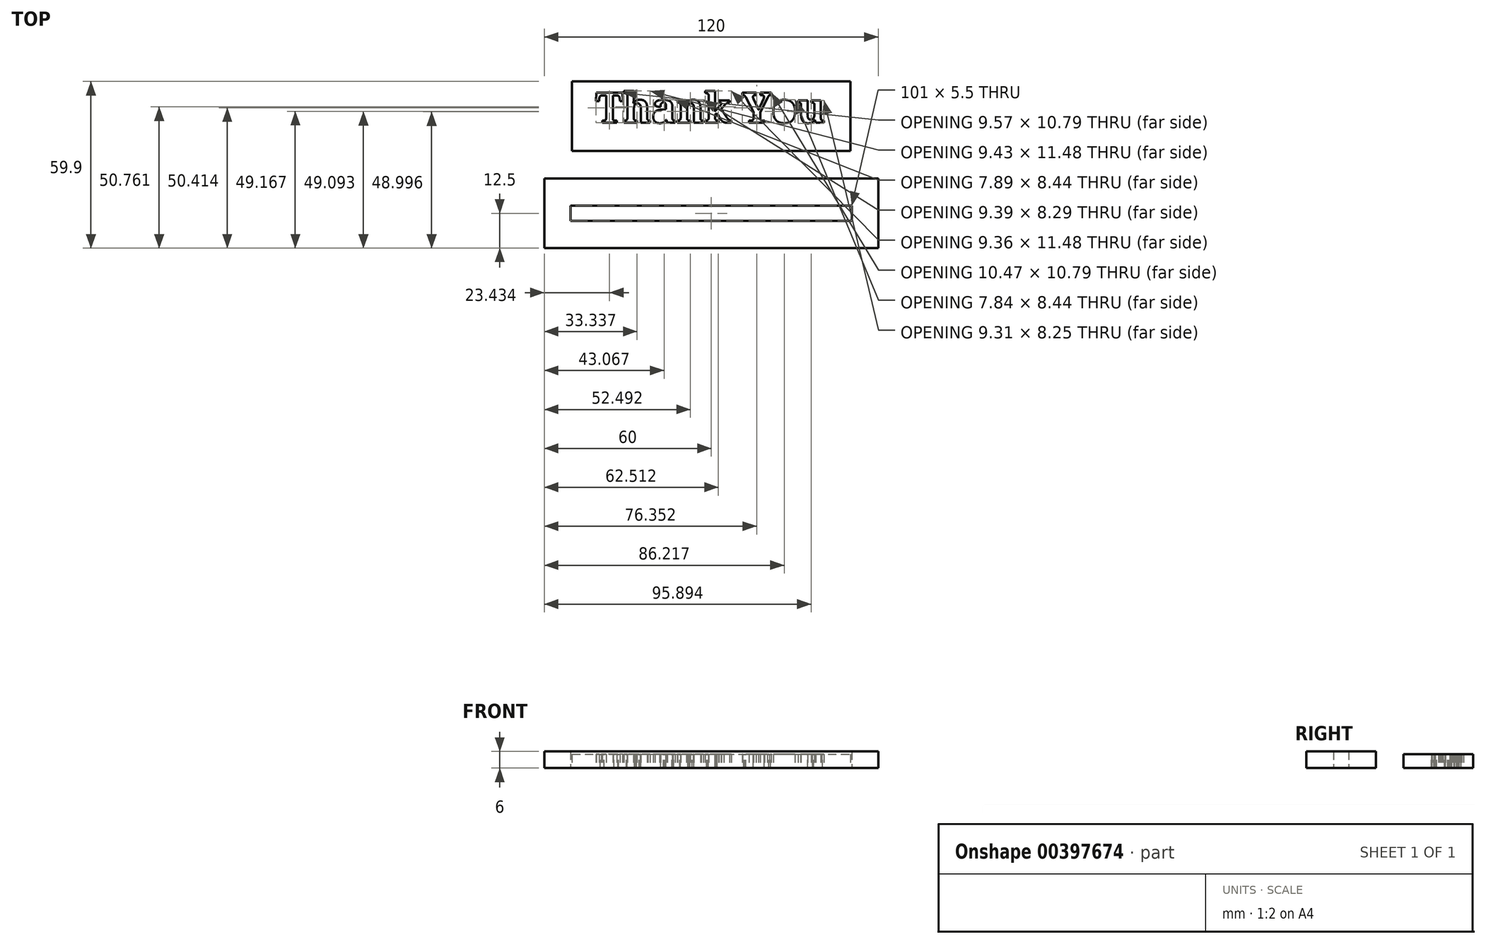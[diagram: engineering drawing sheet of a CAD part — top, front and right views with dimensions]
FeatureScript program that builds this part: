
annotation { "Feature Type Name" : "Feature", "Feature Type Description" : "" }
export const myFeature = defineFeature(function(context is Context, id is Id, definition is map)
    precondition{}
    {
        {
            var Q0;
            Q0=qCreatedBy(makeId("Top.planeOp"),FACE);
            var sketch = newSketch(context, id + "F0", { "sketchPlane" : qUnion([Q0])});
            skLineSegment(sketch, "E0.bottom", {"start": v(-50, 12.5) * mm, "end": v(50, 12.5) * mm});
            skLineSegment(sketch, "E0.top", {"start": v(-50, -12.5) * mm, "end": v(50, -12.5) * mm});
            skLineSegment(sketch, "E0.left", {"start": v(-50, 12.5) * mm, "end": v(-50, -12.5) * mm});
            skLineSegment(sketch, "E0.right", {"start": v(50, 12.5) * mm, "end": v(50, -12.5) * mm});
            skPoint(sketch, "E0.middle", {"position": v(0, 0) * mm});
            skText(sketch, "E1", { "text": "Thank You", "fontName": "NotoSerif-Bold.ttf"});
            const initialGuessF0  = {"E1": [-0.0415, -0.00238, 1, 0, 0.01088]};
            skSetInitialGuess(sketch, initialGuessF0);
            skSolve(sketch);
        }
        {
            var Q0;
            Q0 = qSketchRegion(id + "F0", true);
            extrude(context, id + "F1", {"entities" : qUnion([Q0]), "depth" : 5 * mm});
        }
        {
            var Q0;
            Q0=qCreatedBy(makeId("Top.planeOp"),FACE);
            var sketch = newSketch(context, id + "F2", { "sketchPlane" : qUnion([Q0])});
            skLineSegment(sketch, "E2.bottom", {"start": v(-60, -47.4) * mm, "end": v(60, -47.4) * mm});
            skLineSegment(sketch, "E2.top", {"start": v(-60, -22.4) * mm, "end": v(60, -22.4) * mm});
            skLineSegment(sketch, "E2.left", {"start": v(-60, -47.4) * mm, "end": v(-60, -22.4) * mm});
            skLineSegment(sketch, "E2.right", {"start": v(60, -47.4) * mm, "end": v(60, -22.4) * mm});
            skPoint(sketch, "E2.middle", {"position": v(0, -34.9) * mm});
            skLineSegment(sketch, "E3.bottom", {"start": v(-50.5, -37.65) * mm, "end": v(50.5, -37.65) * mm});
            skLineSegment(sketch, "E3.top", {"start": v(-50.5, -32.15) * mm, "end": v(50.5, -32.15) * mm});
            skLineSegment(sketch, "E3.left", {"start": v(-50.5, -37.65) * mm, "end": v(-50.5, -32.15) * mm});
            skLineSegment(sketch, "E3.right", {"start": v(50.5, -37.65) * mm, "end": v(50.5, -32.15) * mm});
            skSolve(sketch);
        }
        {
            var Q0;
            Q0=makeQuery(id+"F2.imprint","IMPRINT",FACE,{"disambiguationData":[TD([[makeQuery(id+"F2.imprint","IMPRINT",EDGE,{"derivedFrom":sQuery(id+"F2.wireOp",EDGE,"E2.bottom")}),1.0]])]});
            extrude(context, id + "F3", {"entities" : qUnion([Q0]), "depth" : 6 * mm});
        }
    });
